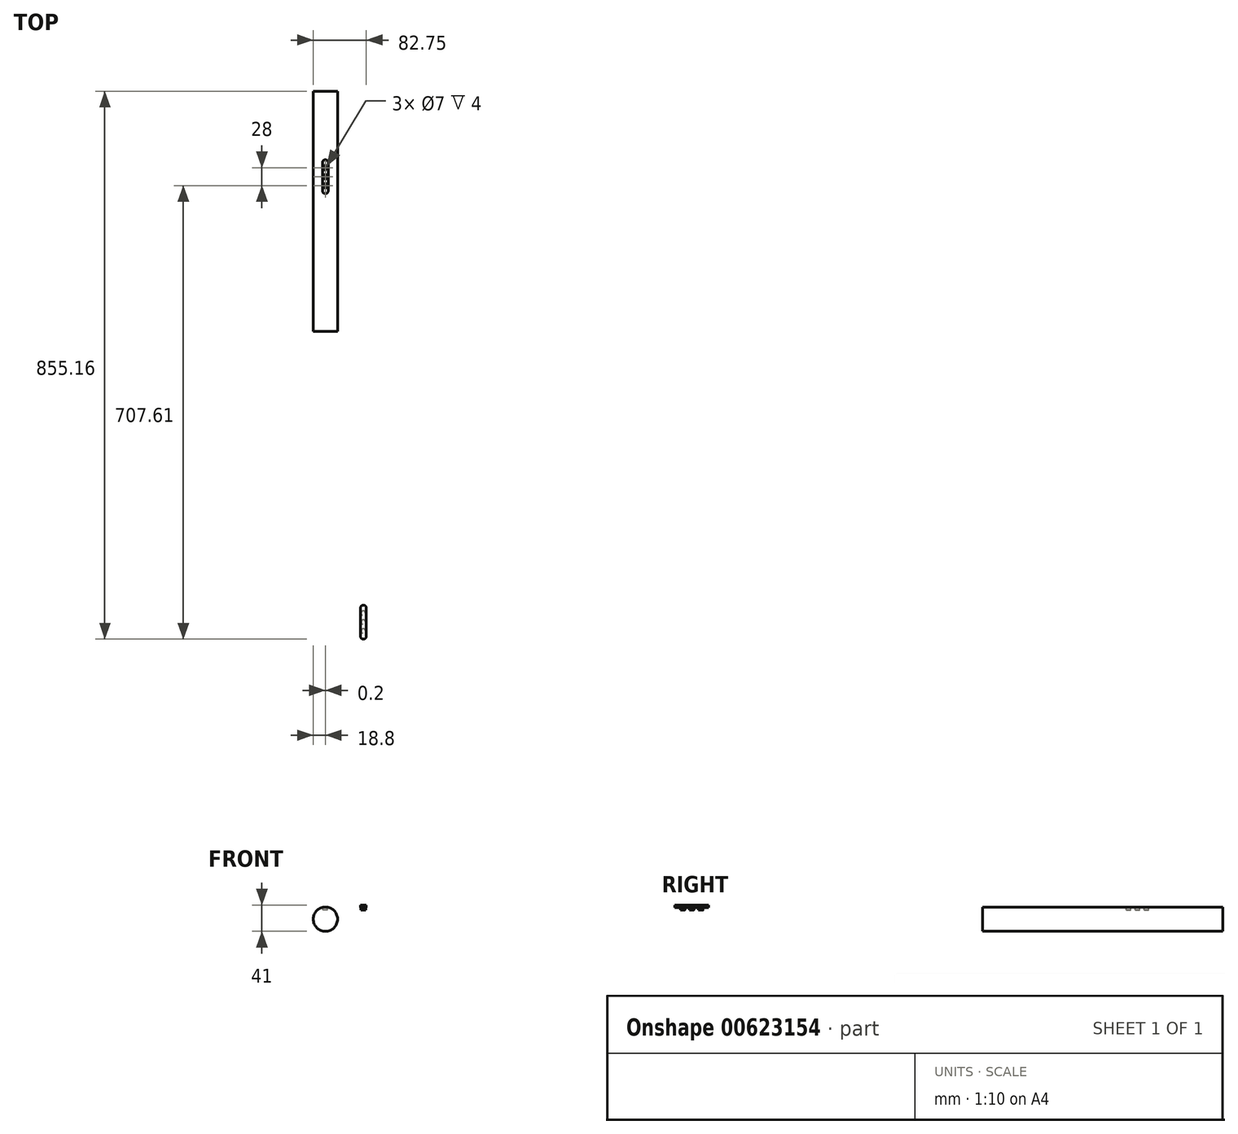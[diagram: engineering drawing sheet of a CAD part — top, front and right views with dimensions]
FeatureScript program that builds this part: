
annotation { "Feature Type Name" : "Feature", "Feature Type Description" : "" }
export const myFeature = defineFeature(function(context is Context, id is Id, definition is map)
    precondition{}
    {
        {
            var Q0;
            Q0=qCreatedBy(makeId("Front.planeOp"),FACE);
            var sketch = newSketch(context, id + "F0", { "sketchPlane" : qUnion([Q0])});
            skCircle(sketch, "E0", {"center": v(0, 0) * mm, "radius": 19 * mm});
            skSolve(sketch);
        }
        {
            var Q0;
            Q0=qSketchRegion(id+"F0",true);
            extrude(context, id + "F1", {"entities" : qUnion([Q0]), "depth" : 375 * mm, "offsetDistance" : 25 * mm});
        }
        {
            var Q0;
            Q0=qCreatedBy(makeId("Top.planeOp"),FACE);
            cPlane(context, id + "F2", {"entities" : qUnion([Q0]), "cplaneType" : CPlaneType.OFFSET, "offset" : 18 * mm, "width" : 150 * mm, "height" : 150 * mm});
        }
        {
            var Q0;
            Q0=qCreatedBy(id+"F2.planeOp",FACE);
            var sketch = newSketch(context, id + "F3", { "sketchPlane" : qUnion([Q0])});
            skLineSegment(sketch, "E1.0", {"start": v(13.2, 0) * mm, "end": v(-13.2, 0) * mm, "construction": true});
            skLineSegment(sketch, "E2", {"start": v(0, 0) * mm, "end": v(0, -133.55) * mm, "construction": true});
            skLineSegment(sketch, "E3.left", {"start": v(4.5, -111.55) * mm, "end": v(4.5, -155.55) * mm});
            skLineSegment(sketch, "E3.right", {"start": v(-4.5, -111.55) * mm, "end": v(-4.5, -155.55) * mm});
            skPoint(sketch, "E3.middle", {"position": v(0, -133.55) * mm});
            skArc(sketch, "E4", {"start": v(-4.5, -111.55) * mm, "mid": v(0, -107.05) * mm, "end": v(4.5, -111.55) * mm});
            skArc(sketch, "E5", {"start": v(-4.5, -155.55) * mm, "mid": v(0, -160.05) * mm, "end": v(4.5, -155.55) * mm});
            skCircle(sketch, "E6", {"center": v(0, -133.55) * mm, "radius": 3.5 * mm, "construction": true});
            skCircle(sketch, "E7", {"center": v(-0.2, -119.55) * mm, "radius": 3.5 * mm, "construction": true});
            skCircle(sketch, "E8", {"center": v(0, -147.55) * mm, "radius": 3.5 * mm, "construction": true});
            skLineSegment(sketch, "E9.0", {"start": v(19, 0) * mm, "end": v(-19, 0) * mm, "construction": true});
            skSolve(sketch);
        }
        {
            var Q0;
            Q0 = qSketchRegion(id + "F3", true);
            extrude(context, id + "F4", {"entities" : qUnion([Q0]), "operationType" : NewBodyOperationType.REMOVE, "depth" : 5 * mm, "offsetDistance" : 25 * mm});
        }
        {
            var Q0;
            Q0=makeQuery(id+"F4.boolean.opBoolean","COPY",FACE,{"derivedFrom":makeQuery(id+"F4.opExtrude","CAP_FACE",FACE,{"disambiguationData":[OSD([sQuery(id+"F3.wireOp",EDGE,"E3.left"),sQuery(id+"F3.wireOp",EDGE,"E3.right"),sQuery(id+"F3.wireOp",EDGE,"E4"),sQuery(id+"F3.wireOp",EDGE,"E5")])],"isStart":true})});
            var sketch = newSketch(context, id + "F5", { "sketchPlane" : qUnion([Q0])});
            skCircle(sketch, "E10.0", {"center": v(0, -147.55) * mm, "radius": 3.5 * mm});
            skCircle(sketch, "E11.0", {"center": v(0, -133.55) * mm, "radius": 3.5 * mm});
            skCircle(sketch, "E12.0", {"center": v(-0.2, -119.55) * mm, "radius": 3.5 * mm});
            skSolve(sketch);
        }
        {
            var Q0;
            Q0 = qSketchRegion(id + "F5", true);
            extrude(context, id + "F6", {"entities" : qUnion([Q0]), "operationType" : NewBodyOperationType.REMOVE, "oppositeDirection" : true, "depth" : 4 * mm, "offsetDistance" : 25 * mm});
        }
        {
            var Q0;
            Q0=qCreatedBy(id+"F2.planeOp",FACE);
            var sketch = newSketch(context, id + "F7", { "sketchPlane" : qUnion([Q0])});
            skLineSegment(sketch, "E13.0", {"start": v(78.25, -695.11) * mm, "end": v(40.25, -695.11) * mm, "construction": true});
            skLineSegment(sketch, "E14", {"start": v(59.25, -695.11) * mm, "end": v(59.25, -828.66) * mm, "construction": true});
            skLineSegment(sketch, "E15.left", {"start": v(63.75, -806.66) * mm, "end": v(63.75, -850.66) * mm});
            skLineSegment(sketch, "E15.right", {"start": v(54.75, -806.66) * mm, "end": v(54.75, -850.66) * mm});
            skPoint(sketch, "E15.middle", {"position": v(59.25, -828.66) * mm});
            skArc(sketch, "E16", {"start": v(54.75, -806.66) * mm, "mid": v(59.25, -802.16) * mm, "end": v(63.75, -806.66) * mm});
            skArc(sketch, "E17", {"start": v(54.75, -850.66) * mm, "mid": v(59.25, -855.16) * mm, "end": v(63.75, -850.66) * mm});
            skCircle(sketch, "E18", {"center": v(59.25, -828.66) * mm, "radius": 3.5 * mm, "construction": true});
            skCircle(sketch, "E19", {"center": v(59.05, -814.66) * mm, "radius": 3.5 * mm, "construction": true});
            skCircle(sketch, "E20", {"center": v(59.25, -842.66) * mm, "radius": 3.5 * mm, "construction": true});
            skSolve(sketch);
        }
        {
            var Q0;
            Q0=makeQuery(id+"F7.imprint","IMPRINT",FACE,{"disambiguationData":[TD([[makeQuery(id+"F7.imprint","IMPRINT",EDGE,{"derivedFrom":sQuery(id+"F7.wireOp",EDGE,"E15.left")}),-1.0]])]});
            extrude(context, id + "F8", {"entities" : qUnion([Q0]), "depth" : 4 * mm, "offsetDistance" : 25 * mm});
        }
        {
            var Q0;
            Q0=makeQuery(id+"F7.imprint","IMPRINT",FACE,{"disambiguationData":[TD([[makeQuery(id+"F7.imprint","IMPRINT",EDGE,{"derivedFrom":sQuery(id+"F7.wireOp",EDGE,"E15.left")}),-1.0]])]});
            var sketch = newSketch(context, id + "F9", { "sketchPlane" : qUnion([Q0])});
            skCircle(sketch, "E21.0", {"center": v(59.25, -842.66) * mm, "radius": 3.5 * mm});
            skCircle(sketch, "E22.0", {"center": v(59.25, -828.66) * mm, "radius": 3.5 * mm});
            skCircle(sketch, "E23.0", {"center": v(59.05, -814.66) * mm, "radius": 3.5 * mm});
            skSolve(sketch);
        }
        {
            var Q0;
            Q0 = qSketchRegion(id + "F9", true);
            extrude(context, id + "F10", {"entities" : qUnion([Q0]), "operationType" : NewBodyOperationType.ADD, "oppositeDirection" : true, "depth" : 4 * mm, "offsetDistance" : 25 * mm});
        }
    });
